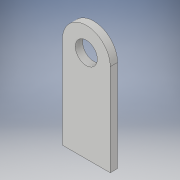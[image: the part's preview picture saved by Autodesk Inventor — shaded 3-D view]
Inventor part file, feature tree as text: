
AUTODESK INVENTOR PART (.ipt)
format: ipt  version: 2019 (Build 230136000, 136)  size: 107,520 bytes
history: native  units: mm
features: other x1, sketch x1, extrude x1, fillet x1, hole x1
ambient origin geometry x8: Origin, YZ Plane, XZ Plane, XY Plane, X Axis, Y Axis, Z Axis, Center Point
bodies: Body1 (feature_tree)
feature tree (5):
  other  "Bryła1"
  sketch  "Szkic1"
  extrude  "Wyciągnięcie proste1"  Depth=6.5mm
  fillet  "Zaokrąglenie1"  Radius=1.0mm
  hole  "Otwór1"  [1 undecoded]
note: 1 required parameter value undecoded (feature->parameter linkage not recoverable at this tier; creation-order binding heuristic only, values carry confidence <= 0.55)
